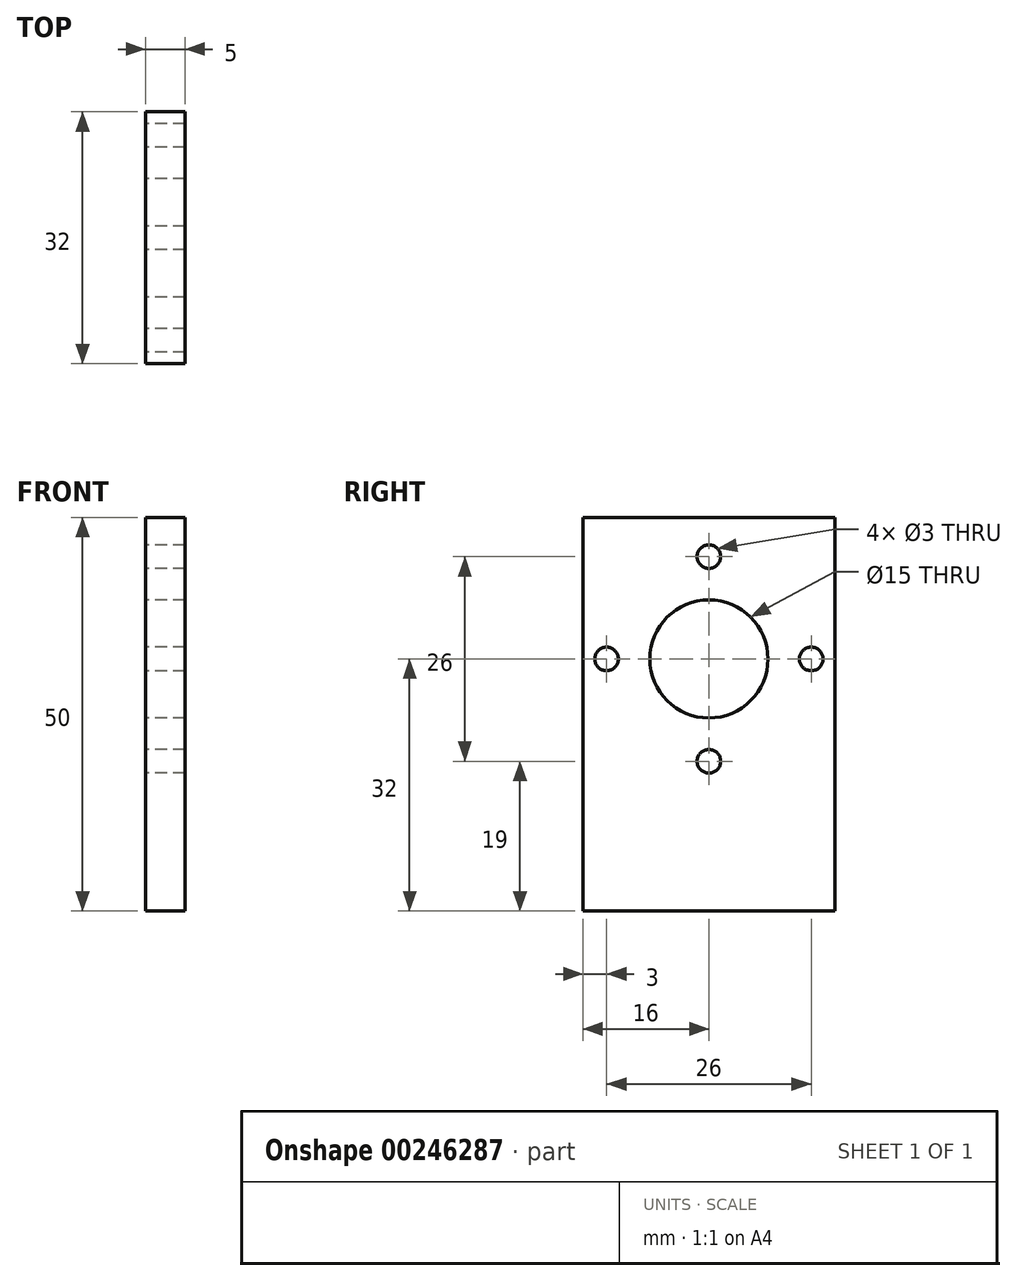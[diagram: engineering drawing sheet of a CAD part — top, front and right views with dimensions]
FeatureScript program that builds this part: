
annotation { "Feature Type Name" : "Feature", "Feature Type Description" : "" }
export const myFeature = defineFeature(function(context is Context, id is Id, definition is map)
    precondition{}
    {
        {
            var Q0;
            Q0=qCreatedBy(makeId("Right.planeOp"),FACE);
            var sketch = newSketch(context, id + "F0", { "sketchPlane" : qUnion([Q0])});
            skLineSegment(sketch, "E0.bottom", {"start": v(-16, 18) * mm, "end": v(16, 18) * mm});
            skLineSegment(sketch, "E0.top", {"start": v(-16, -32) * mm, "end": v(16, -32) * mm});
            skLineSegment(sketch, "E0.left", {"start": v(-16, 18) * mm, "end": v(-16, -32) * mm});
            skLineSegment(sketch, "E0.right", {"start": v(16, 18) * mm, "end": v(16, -32) * mm});
            skPoint(sketch, "E1", {"position": v(0, 18) * mm});
            skCircle(sketch, "E2", {"center": v(0, 0) * mm, "radius": 13 * mm, "construction": true});
            skCircle(sketch, "E3", {"center": v(0, 13) * mm, "radius": 1.5 * mm});
            skCircle(sketch, "E4", {"center": v(-13, 0) * mm, "radius": 1.5 * mm});
            skCircle(sketch, "E5", {"center": v(0, -13) * mm, "radius": 1.5 * mm});
            skCircle(sketch, "E6", {"center": v(13, 0) * mm, "radius": 1.5 * mm});
            skCircle(sketch, "E7", {"center": v(0, 0) * mm, "radius": 7.5 * mm});
            skSolve(sketch);
        }
        {
            var Q0;
            Q0=makeQuery(id+"F0.imprint","IMPRINT",FACE,{"disambiguationData":[TD([[makeQuery(id+"F0.imprint","IMPRINT",EDGE,{"derivedFrom":sQuery(id+"F0.wireOp",EDGE,"E0.bottom")}),-1.0]])]});
            extrude(context, id + "F1", {"entities" : qUnion([Q0]), "depth" : 5 * mm});
        }
    });
